# Revit family: Magnuson-KP_Screen
name_source: partatom
category: Furniture
revit_build: Autodesk Revit 2014 (Build: 20140709_2115(x64)
units: mm (PartAtom-declared; Revit-internal decimal feet)

## types (4) — shared parameters
Assembly Code = E2020200
CAP = MG - UHMW, Black
Depth = 1.084 "
FRAME = MG - Aluminum
Height = 64.125 "
Keynote = 12500
Manufacturer = Magnuson Group
Type Comments = KP SCREENS
URL = www.magnusongroup.com

## per-type parameters (varying)
| type | Description | Model | SCREEN | Width |
| KP 1608 T | Screen, 31"x64", Fabric | KP 1608 T
KP 1608 T
KP 1608 T | MG - Linen, Beige | 31.89 " |
| KP 1612 T | Screen, 48"x64", Fabric | KP 1612 T | MG - Linen, Beige | 47.913 " |
| KP 1608 PC | Screen, 31"x64", Polycarbonate | KP 1608 PC | MG - Polycarbonate, Clear | 31.89 " |
| KP 1612 PC | Screen, 48"x64", Polycarbonate | KP 1612 PC | MG - Polycarbonate, Clear | 47.913 " |

## geometry (parser evidence)
native form markers: Sweep x1
no freeform markers — native parametric forms only
